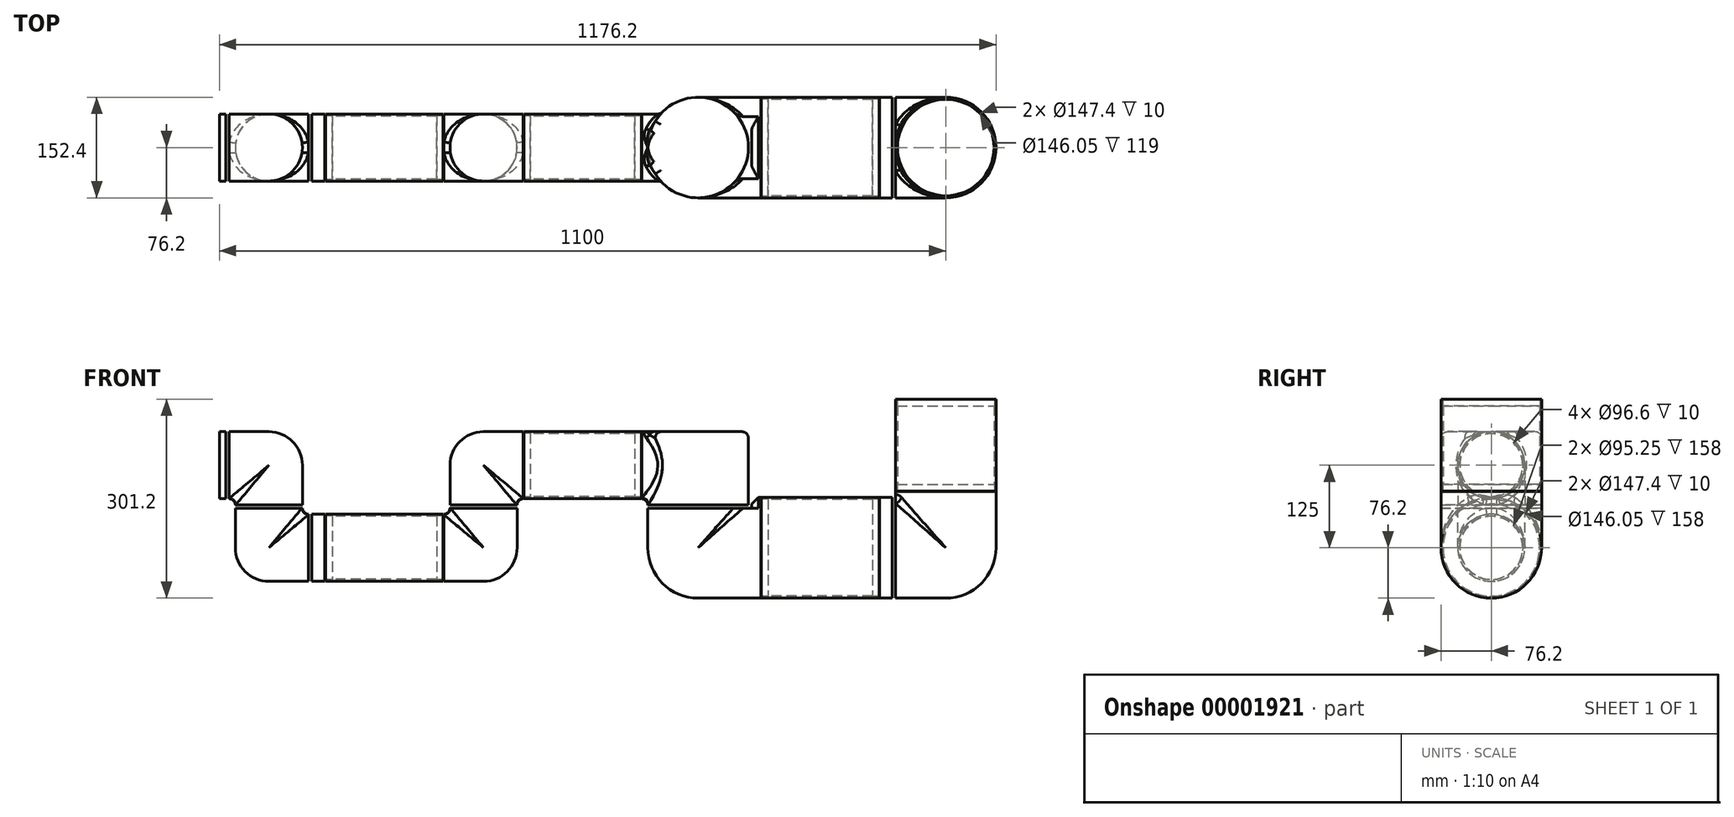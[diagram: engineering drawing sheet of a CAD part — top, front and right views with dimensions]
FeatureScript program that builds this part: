
annotation { "Feature Type Name" : "Feature", "Feature Type Description" : "" }
export const myFeature = defineFeature(function(context is Context, id is Id, definition is map)
    precondition{}
    {
        {
            var Q0;
            Q0=qCreatedBy(makeId("Front.planeOp"),FACE);
            var sketch = newSketch(context, id + "F0", { "sketchPlane" : qUnion([Q0])});
            skLineSegment(sketch, "E0", {"start": v(0, 0) * mm, "end": v(0, -225) * mm, "construction": true});
            skLineSegment(sketch, "E1", {"start": v(0, -225) * mm, "end": v(-375, -225) * mm, "construction": true});
            skLineSegment(sketch, "E2", {"start": v(-375, -225) * mm, "end": v(-375, -100) * mm, "construction": true});
            skLineSegment(sketch, "E3", {"start": v(-375, -100) * mm, "end": v(-700, -100) * mm, "construction": true});
            skLineSegment(sketch, "E4", {"start": v(-700, -100) * mm, "end": v(-700, -225) * mm, "construction": true});
            skLineSegment(sketch, "E5", {"start": v(-700, -225) * mm, "end": v(-1025, -225) * mm, "construction": true});
            skLineSegment(sketch, "E6", {"start": v(-1025, -225) * mm, "end": v(-1025, -100) * mm, "construction": true});
            skLineSegment(sketch, "E7", {"start": v(-1025, -100) * mm, "end": v(-1100, -100) * mm, "construction": true});
            skSolve(sketch);
        }
        {
            var Q0;
            Q0=qCreatedBy(makeId("Top.planeOp"),FACE);
            var Q1;
            Q1=sQuery(id+"F0.wireOp",VERTEX,"E1.start");
            cPlane(context, id + "F1", {"entities" : qUnion([Q0, Q1]), "cplaneType" : CPlaneType.PLANE_POINT, "offset" : 152.4 * mm, "width" : 152.4 * mm, "height" : 152.4 * mm});
        }
        {
            var Q0;
            Q0=qCreatedBy(makeId("Right.planeOp"),FACE);
            var Q1;
            Q1=sQuery(id+"F0.wireOp",VERTEX,"E2.start");
            cPlane(context, id + "F2", {"entities" : qUnion([Q0, Q1]), "cplaneType" : CPlaneType.PLANE_POINT, "offset" : 152.4 * mm, "width" : 152.4 * mm, "height" : 152.4 * mm});
        }
        {
            var Q0;
            Q0=qCreatedBy(makeId("Top.planeOp"),FACE);
            var Q1;
            Q1=sQuery(id+"F0.wireOp",VERTEX,"E3.start");
            cPlane(context, id + "F3", {"entities" : qUnion([Q0, Q1]), "cplaneType" : CPlaneType.PLANE_POINT, "offset" : 152.4 * mm, "width" : 152.4 * mm, "height" : 152.4 * mm});
        }
        {
            var Q0;
            Q0=qCreatedBy(makeId("Right.planeOp"),FACE);
            var Q1;
            Q1=sQuery(id+"F0.wireOp",VERTEX,"E4.end");
            cPlane(context, id + "F4", {"entities" : qUnion([Q0, Q1]), "cplaneType" : CPlaneType.PLANE_POINT, "offset" : 152.4 * mm, "width" : 152.4 * mm, "height" : 152.4 * mm});
        }
        {
            var Q0;
            Q0=qCreatedBy(makeId("Top.planeOp"),FACE);
            var Q1;
            Q1=sQuery(id+"F0.wireOp",VERTEX,"E4.end");
            cPlane(context, id + "F5", {"entities" : qUnion([Q0, Q1]), "cplaneType" : CPlaneType.PLANE_POINT, "offset" : 152.4 * mm, "width" : 152.4 * mm, "height" : 152.4 * mm});
        }
        {
            var Q0;
            Q0=qCreatedBy(makeId("Right.planeOp"),FACE);
            var Q1;
            Q1=sQuery(id+"F0.wireOp",VERTEX,"E6.start");
            cPlane(context, id + "F6", {"entities" : qUnion([Q0, Q1]), "cplaneType" : CPlaneType.PLANE_POINT, "offset" : 152.4 * mm, "width" : 152.4 * mm, "height" : 152.4 * mm});
        }
        {
            var Q0;
            Q0=qCreatedBy(makeId("Top.planeOp"),FACE);
            var Q1;
            Q1=sQuery(id+"F0.wireOp",VERTEX,"E6.end");
            cPlane(context, id + "F7", {"entities" : qUnion([Q0, Q1]), "cplaneType" : CPlaneType.PLANE_POINT, "offset" : 152.4 * mm, "width" : 152.4 * mm, "height" : 152.4 * mm});
        }
        {
            var Q0;
            Q0=qCreatedBy(makeId("Right.planeOp"),FACE);
            var Q1;
            Q1=sQuery(id+"F0.wireOp",VERTEX,"E7.end");
            cPlane(context, id + "F8", {"entities" : qUnion([Q0, Q1]), "cplaneType" : CPlaneType.PLANE_POINT, "offset" : 152.4 * mm, "width" : 152.4 * mm, "height" : 152.4 * mm});
        }
        {
            var Q0;
            Q0=qCreatedBy(makeId("Top.planeOp"),FACE);
            var sketch = newSketch(context, id + "F9", { "sketchPlane" : qUnion([Q0])});
            skCircle(sketch, "E8", {"center": v(0, 0) * mm, "radius": 76.2 * mm});
            skSolve(sketch);
        }
        {
            var Q0;
            Q0=makeQuery(id+"F9.imprint","IMPRINT",FACE,{"disambiguationData":[TD([[makeQuery(id+"F9.imprint","IMPRINT",EDGE,{"derivedFrom":sQuery(id+"F9.wireOp",EDGE,"E8")}),1.0]])]});
            var Q1;
            Q1=qCreatedBy(id+"F1.planeOp",FACE);
            extrude(context, id + "F10", {"entities" : qUnion([Q0]), "endBound" : BoundingType.UP_TO_SURFACE, "oppositeDirection" : true, "endBoundEntityFace" : qUnion([Q1]), "depth" : 25.4 * mm});
        }
        {
            var Q0;
            Q0=qCreatedBy(makeId("Right.planeOp"),FACE);
            var sketch = newSketch(context, id + "F11", { "sketchPlane" : qUnion([Q0])});
            skCircle(sketch, "E9", {"center": v(0, -225) * mm, "radius": 76.2 * mm});
            skSolve(sketch);
        }
        {
            var Q0;
            Q0 = qSketchRegion(id + "F11", true);
            var Q1;
            Q1=qCreatedBy(id+"F2.planeOp",FACE);
            extrude(context, id + "F12", {"entities" : qUnion([Q0]), "operationType" : NewBodyOperationType.ADD, "endBound" : BoundingType.UP_TO_SURFACE, "oppositeDirection" : true, "endBoundEntityFace" : qUnion([Q1]), "depth" : 25.4 * mm});
        }
        {
            var Q0;
            Q0=qCreatedBy(id+"F1.planeOp",FACE);
            var sketch = newSketch(context, id + "F13", { "sketchPlane" : qUnion([Q0])});
            skCircle(sketch, "E10", {"center": v(-375, 0) * mm, "radius": 76.2 * mm});
            skSolve(sketch);
        }
        {
            var Q0;
            Q0=makeQuery(id+"F13.imprint","IMPRINT",FACE,{"disambiguationData":[TD([[makeQuery(id+"F13.imprint","IMPRINT",EDGE,{"derivedFrom":sQuery(id+"F13.wireOp",EDGE,"E10")}),1.0]])]});
            var Q1;
            Q1=qCreatedBy(id+"F3.planeOp",FACE);
            extrude(context, id + "F14", {"entities" : qUnion([Q0]), "operationType" : NewBodyOperationType.ADD, "endBound" : BoundingType.UP_TO_SURFACE, "endBoundEntityFace" : qUnion([Q1]), "depth" : 25.4 * mm});
        }
        {
            var Q0;
            Q0=qCreatedBy(id+"F2.planeOp",FACE);
            var sketch = newSketch(context, id + "F15", { "sketchPlane" : qUnion([Q0])});
            skCircle(sketch, "E11", {"center": v(0, -100) * mm, "radius": 50.8 * mm});
            skSolve(sketch);
        }
        {
            var Q0;
            Q0 = qSketchRegion(id + "F15", true);
            var Q1;
            Q1=qCreatedBy(id+"F4.planeOp",FACE);
            extrude(context, id + "F16", {"entities" : qUnion([Q0]), "operationType" : NewBodyOperationType.ADD, "endBound" : BoundingType.UP_TO_SURFACE, "oppositeDirection" : true, "endBoundEntityFace" : qUnion([Q1]), "depth" : 25.4 * mm});
        }
        {
            var Q0;
            Q0=qCreatedBy(id+"F3.planeOp",FACE);
            var sketch = newSketch(context, id + "F17", { "sketchPlane" : qUnion([Q0])});
            skCircle(sketch, "E12", {"center": v(-700, 0) * mm, "radius": 50.8 * mm});
            skSolve(sketch);
        }
        {
            var Q0;
            Q0 = qSketchRegion(id + "F17", true);
            var Q1;
            Q1=qCreatedBy(id+"F5.planeOp",FACE);
            extrude(context, id + "F18", {"entities" : qUnion([Q0]), "operationType" : NewBodyOperationType.ADD, "endBound" : BoundingType.UP_TO_SURFACE, "oppositeDirection" : true, "endBoundEntityFace" : qUnion([Q1]), "depth" : 25.4 * mm});
        }
        {
            var Q0;
            Q0=qCreatedBy(id+"F4.planeOp",FACE);
            var sketch = newSketch(context, id + "F19", { "sketchPlane" : qUnion([Q0])});
            skCircle(sketch, "E13", {"center": v(0, -225) * mm, "radius": 50.8 * mm});
            skSolve(sketch);
        }
        {
            var Q0;
            Q0 = qSketchRegion(id + "F19", true);
            var Q1;
            Q1=qCreatedBy(id+"F6.planeOp",FACE);
            extrude(context, id + "F20", {"entities" : qUnion([Q0]), "operationType" : NewBodyOperationType.ADD, "endBound" : BoundingType.UP_TO_SURFACE, "oppositeDirection" : true, "endBoundEntityFace" : qUnion([Q1]), "depth" : 25.4 * mm});
        }
        {
            var Q0;
            Q0=qCreatedBy(id+"F5.planeOp",FACE);
            var sketch = newSketch(context, id + "F21", { "sketchPlane" : qUnion([Q0])});
            skCircle(sketch, "E14", {"center": v(-1025, 0) * mm, "radius": 50.8 * mm});
            skSolve(sketch);
        }
        {
            var Q0;
            Q0 = qSketchRegion(id + "F21", true);
            var Q1;
            Q1=qCreatedBy(id+"F7.planeOp",FACE);
            extrude(context, id + "F22", {"entities" : qUnion([Q0]), "operationType" : NewBodyOperationType.ADD, "endBound" : BoundingType.UP_TO_SURFACE, "endBoundEntityFace" : qUnion([Q1]), "depth" : 25.4 * mm});
        }
        {
            var Q0;
            Q0=qCreatedBy(id+"F6.planeOp",FACE);
            var sketch = newSketch(context, id + "F23", { "sketchPlane" : qUnion([Q0])});
            skCircle(sketch, "E15", {"center": v(0, -100) * mm, "radius": 50.8 * mm});
            skSolve(sketch);
        }
        {
            var Q0;
            Q0 = qSketchRegion(id + "F23", true);
            var Q1;
            Q1=qCreatedBy(id+"F8.planeOp",FACE);
            extrude(context, id + "F24", {"entities" : qUnion([Q0]), "operationType" : NewBodyOperationType.ADD, "endBound" : BoundingType.UP_TO_SURFACE, "oppositeDirection" : true, "endBoundEntityFace" : qUnion([Q1]), "depth" : 25.4 * mm});
        }
        {
            var Q0;
            Q0=makeQuery(id+"F10.opExtrude","CAP_FACE",FACE,{"disambiguationData":[OSD([sQuery(id+"F9.wireOp",EDGE,"E8")])],"isStart":false});
            var Q1;
            Q1=makeQuery(id+"F12.boolean.opBoolean","INTERSECT",EDGE,{"derivedFrom":[makeQuery(id+"F10.opExtrude","CAP_FACE",FACE,{"disambiguationData":[OSD([sQuery(id+"F9.wireOp",EDGE,"E8")])],"isStart":false}),makeQuery(id+"F12.opExtrude","CAP_FACE",FACE,{"disambiguationData":[OSD([sQuery(id+"F11.wireOp",EDGE,"E9")])],"isStart":true})]});
            revolve(context, id + "F25", {"operationType" : NewBodyOperationType.ADD, "entities" : qUnion([Q0]), "axis" : qUnion([Q1]), "revolveType" : RevolveType.ONE_DIRECTION, "angle" : 90 * degree});
        }
        {
            var Q0;
            Q0=makeQuery(id+"F12.opExtrude","CAP_FACE",FACE,{"disambiguationData":[OSD([sQuery(id+"F11.wireOp",EDGE,"E9")])],"isStart":false});
            var Q1;
            Q1=makeQuery(id+"F14.boolean.opBoolean","INTERSECT",EDGE,{"derivedFrom":[makeQuery(id+"F12.opExtrude","CAP_FACE",FACE,{"disambiguationData":[OSD([sQuery(id+"F11.wireOp",EDGE,"E9")])],"isStart":false}),makeQuery(id+"F14.opExtrude","CAP_FACE",FACE,{"disambiguationData":[OSD([sQuery(id+"F13.wireOp",EDGE,"E10")])],"isStart":true})]});
            revolve(context, id + "F26", {"operationType" : NewBodyOperationType.ADD, "entities" : qUnion([Q0]), "axis" : qUnion([Q1]), "revolveType" : RevolveType.ONE_DIRECTION, "oppositeDirection" : true, "angle" : 90 * degree});
        }
        {
            var Q0;
            Q0=makeQuery(id+"F16.opExtrude","CAP_FACE",FACE,{"disambiguationData":[OSD([sQuery(id+"F15.wireOp",EDGE,"E11")])],"isStart":false});
            var Q1;
            Q1=makeQuery(id+"F18.boolean.opBoolean","INTERSECT",EDGE,{"derivedFrom":[makeQuery(id+"F16.opExtrude","CAP_FACE",FACE,{"disambiguationData":[OSD([sQuery(id+"F15.wireOp",EDGE,"E11")])],"isStart":false}),makeQuery(id+"F18.opExtrude","CAP_FACE",FACE,{"disambiguationData":[OSD([sQuery(id+"F17.wireOp",EDGE,"E12")])],"isStart":true})]});
            revolve(context, id + "F27", {"operationType" : NewBodyOperationType.ADD, "entities" : qUnion([Q0]), "axis" : qUnion([Q1]), "revolveType" : RevolveType.ONE_DIRECTION, "angle" : 90 * degree});
        }
        {
            var Q0;
            Q0=makeQuery(id+"F18.opExtrude","CAP_FACE",FACE,{"disambiguationData":[OSD([sQuery(id+"F17.wireOp",EDGE,"E12")])],"isStart":false});
            var Q1;
            Q1=makeQuery(id+"F20.boolean.opBoolean","INTERSECT",EDGE,{"derivedFrom":[makeQuery(id+"F18.opExtrude","CAP_FACE",FACE,{"disambiguationData":[OSD([sQuery(id+"F17.wireOp",EDGE,"E12")])],"isStart":false}),makeQuery(id+"F20.opExtrude","CAP_FACE",FACE,{"disambiguationData":[OSD([sQuery(id+"F19.wireOp",EDGE,"E13")])],"isStart":true})]});
            revolve(context, id + "F28", {"operationType" : NewBodyOperationType.ADD, "entities" : qUnion([Q0]), "axis" : qUnion([Q1]), "revolveType" : RevolveType.ONE_DIRECTION, "angle" : 90 * degree});
        }
        {
            var Q0;
            Q0=makeQuery(id+"F20.opExtrude","CAP_FACE",FACE,{"disambiguationData":[OSD([sQuery(id+"F19.wireOp",EDGE,"E13")])],"isStart":false});
            var Q1;
            Q1=makeQuery(id+"F22.boolean.opBoolean","INTERSECT",EDGE,{"derivedFrom":[makeQuery(id+"F20.opExtrude","CAP_FACE",FACE,{"disambiguationData":[OSD([sQuery(id+"F19.wireOp",EDGE,"E13")])],"isStart":false}),makeQuery(id+"F22.opExtrude","CAP_FACE",FACE,{"disambiguationData":[OSD([sQuery(id+"F21.wireOp",EDGE,"E14")])],"isStart":true})]});
            revolve(context, id + "F29", {"operationType" : NewBodyOperationType.ADD, "entities" : qUnion([Q0]), "axis" : qUnion([Q1]), "revolveType" : RevolveType.ONE_DIRECTION, "oppositeDirection" : true, "angle" : 90 * degree});
        }
        {
            var Q0;
            Q0=makeQuery(id+"F22.opExtrude","CAP_FACE",FACE,{"disambiguationData":[OSD([sQuery(id+"F21.wireOp",EDGE,"E14")])],"isStart":false});
            var Q1;
            Q1=makeQuery(id+"F24.boolean.opBoolean","INTERSECT",EDGE,{"derivedFrom":[makeQuery(id+"F22.opExtrude","CAP_FACE",FACE,{"disambiguationData":[OSD([sQuery(id+"F21.wireOp",EDGE,"E14")])],"isStart":false}),makeQuery(id+"F24.opExtrude","CAP_FACE",FACE,{"disambiguationData":[OSD([sQuery(id+"F23.wireOp",EDGE,"E15")])],"isStart":true})]});
            revolve(context, id + "F30", {"operationType" : NewBodyOperationType.ADD, "entities" : qUnion([Q0]), "axis" : qUnion([Q1]), "revolveType" : RevolveType.ONE_DIRECTION, "oppositeDirection" : true, "angle" : 90 * degree});
        }
        {
            var Q0;
            Q0=qCreatedBy(id+"F3.planeOp",FACE);
            var sketch = newSketch(context, id + "F31", { "sketchPlane" : qUnion([Q0])});
            skCircle(sketch, "E16", {"center": v(-375, 0) * mm, "radius": 76.2 * mm});
            skSolve(sketch);
        }
        {
            var Q0;
            Q0 = qSketchRegion(id + "F31", true);
            var Q1;
            Q1=makeQuery(id+"F16.opExtrude","SWEPT_FACE",FACE,{"disambiguationData":[OSD([sQuery(id+"F15.wireOp",EDGE,"E11")])]});
            extrude(context, id + "F32", {"entities" : qUnion([Q0]), "operationType" : NewBodyOperationType.ADD, "endBoundEntity" : qUnion([Q1]), "depth" : 50.8 * mm});
        }
        {
            var Q0;
            Q0=qCreatedBy(makeId("Front.planeOp"),FACE);
            var sketch = newSketch(context, id + "F33", { "sketchPlane" : qUnion([Q0])});
            skLineSegment(sketch, "E17.bottom", {"start": v(-81.2, -225) * mm, "end": v(-76.2, -225) * mm});
            skLineSegment(sketch, "E17.top", {"start": v(-81.2, -301.2) * mm, "end": v(-76.2, -301.2) * mm});
            skLineSegment(sketch, "E17.left", {"start": v(-81.2, -225) * mm, "end": v(-81.2, -301.2) * mm});
            skLineSegment(sketch, "E17.right", {"start": v(-76.2, -225) * mm, "end": v(-76.2, -301.2) * mm});
            skLineSegment(sketch, "E18.bottom", {"start": v(-451.2, -160) * mm, "end": v(-375, -160) * mm});
            skLineSegment(sketch, "E18.top", {"start": v(-451.2, -165) * mm, "end": v(-375, -165) * mm});
            skLineSegment(sketch, "E18.left", {"start": v(-451.2, -160) * mm, "end": v(-451.2, -165) * mm});
            skLineSegment(sketch, "E18.right", {"start": v(-375, -160) * mm, "end": v(-375, -165) * mm});
            skLineSegment(sketch, "E19.bottom", {"start": v(-700, -160) * mm, "end": v(-649.2, -160) * mm});
            skLineSegment(sketch, "E19.top", {"start": v(-700, -165) * mm, "end": v(-649.2, -165) * mm});
            skLineSegment(sketch, "E19.left", {"start": v(-700, -160) * mm, "end": v(-700, -165) * mm});
            skLineSegment(sketch, "E19.right", {"start": v(-649.2, -160) * mm, "end": v(-649.2, -165) * mm});
            skLineSegment(sketch, "E20.bottom", {"start": v(-960, -225) * mm, "end": v(-965, -225) * mm});
            skLineSegment(sketch, "E20.top", {"start": v(-960, -174.2) * mm, "end": v(-965, -174.2) * mm});
            skLineSegment(sketch, "E20.left", {"start": v(-960, -225) * mm, "end": v(-960, -174.2) * mm});
            skLineSegment(sketch, "E20.right", {"start": v(-965, -225) * mm, "end": v(-965, -174.2) * mm});
            skLineSegment(sketch, "E21.bottom", {"start": v(-1075.8, -160) * mm, "end": v(-1025, -160) * mm});
            skLineSegment(sketch, "E21.top", {"start": v(-1075.8, -165) * mm, "end": v(-1025, -165) * mm});
            skLineSegment(sketch, "E21.left", {"start": v(-1075.8, -160) * mm, "end": v(-1075.8, -165) * mm});
            skLineSegment(sketch, "E21.right", {"start": v(-1025, -160) * mm, "end": v(-1025, -165) * mm});
            skLineSegment(sketch, "E22.bottom", {"start": v(-1090, -100) * mm, "end": v(-1085, -100) * mm});
            skLineSegment(sketch, "E22.top", {"start": v(-1090, -49.2) * mm, "end": v(-1085, -49.2) * mm});
            skLineSegment(sketch, "E22.left", {"start": v(-1090, -100) * mm, "end": v(-1090, -49.2) * mm});
            skLineSegment(sketch, "E22.right", {"start": v(-1085, -100) * mm, "end": v(-1085, -49.2) * mm});
            skLineSegment(sketch, "E23.0", {"start": v(0, -148.8) * mm, "end": v(0, -301.2) * mm, "construction": true});
            skLineSegment(sketch, "E24.0", {"start": v(-76.2, 0) * mm, "end": v(76.2, 0) * mm, "construction": true});
            skLineSegment(sketch, "E25.0", {"start": v(-451.2, -225) * mm, "end": v(-298.8, -225) * mm, "construction": true});
            skLineSegment(sketch, "E26.0", {"start": v(-700, -174.2) * mm, "end": v(-700, -275.8) * mm, "construction": true});
            skLineSegment(sketch, "E27.0", {"start": v(-1075.8, -225) * mm, "end": v(-974.2, -225) * mm, "construction": true});
            skLineSegment(sketch, "E28.0", {"start": v(-1025, -49.2) * mm, "end": v(-1025, -150.8) * mm, "construction": true});
            skLineSegment(sketch, "E29.0", {"start": v(-750.8, -100) * mm, "end": v(-649.2, -100) * mm, "construction": true});
            skSolve(sketch);
        }
        {
            var Q0;
            Q0=makeQuery(id+"F33.imprint","IMPRINT",FACE,{"disambiguationData":[TD([[makeQuery(id+"F33.imprint","IMPRINT",EDGE,{"derivedFrom":sQuery(id+"F33.wireOp",EDGE,"E17.bottom")}),-1.0]])]});
            var Q1;
            Q1=sQuery(id+"F0.wireOp",EDGE,"E1");
            revolve(context, id + "F34", {"operationType" : NewBodyOperationType.REMOVE, "entities" : qUnion([Q0]), "axis" : qUnion([Q1]), "revolveType" : RevolveType.FULL, "oppositeDirection" : true});
        }
        {
            var Q0;
            Q0=makeQuery(id+"F33.imprint","IMPRINT",FACE,{"disambiguationData":[TD([[makeQuery(id+"F33.imprint","IMPRINT",EDGE,{"derivedFrom":sQuery(id+"F33.wireOp",EDGE,"E18.bottom")}),-1.0]])]});
            var Q1;
            Q1=sQuery(id+"F0.wireOp",EDGE,"E2");
            revolve(context, id + "F35", {"operationType" : NewBodyOperationType.REMOVE, "entities" : qUnion([Q0]), "axis" : qUnion([Q1]), "revolveType" : RevolveType.FULL, "oppositeDirection" : true});
        }
        {
            var Q0;
            Q0=qCreatedBy(id+"F3.planeOp",FACE);
            var sketch = newSketch(context, id + "F36", { "sketchPlane" : qUnion([Q0])});
            skCircle(sketch, "E30", {"center": v(-375, 0) * mm, "radius": 76.2 * mm});
            skLineSegment(sketch, "E31.bottom", {"start": v(-375, 159.28) * mm, "end": v(-293.8, 159.28) * mm});
            skLineSegment(sketch, "E31.top", {"start": v(-375, -164.24) * mm, "end": v(-293.8, -164.24) * mm});
            skLineSegment(sketch, "E31.left", {"start": v(-375, 159.28) * mm, "end": v(-375, -164.24) * mm});
            skLineSegment(sketch, "E31.right", {"start": v(-293.8, 159.28) * mm, "end": v(-293.8, -164.24) * mm});
            skSolve(sketch);
        }
        {
            var Q0;
            {var subQ5=sQuery(id+"F36.wireOp",EDGE,"E31.bottom");Q0=makeQuery(id+"F36.imprint","IMPRINT",FACE,{"disambiguationData":[TD([[makeQuery(id+"F36.imprint","IMPRINT",EDGE,{"derivedFrom":subQ5}),-1.0]])]});}
            var Q1;
            Q1=makeQuery(id+"F35.boolean.opBoolean","COPY",FACE,{"derivedFrom":makeQuery(id+"F35.opRevolve","SWEPT_FACE",FACE,{"disambiguationData":[OSD([sQuery(id+"F33.wireOp",EDGE,"E18.top")])]})});
            extrude(context, id + "F37", {"entities" : qUnion([Q0]), "operationType" : NewBodyOperationType.REMOVE, "endBound" : BoundingType.UP_TO_SURFACE, "oppositeDirection" : true, "endBoundEntityFace" : qUnion([Q1]), "depth" : 25 * mm});
        }
        {
            var Q0;
            Q0=makeQuery(id+"F33.imprint","IMPRINT",FACE,{"disambiguationData":[TD([[makeQuery(id+"F33.imprint","IMPRINT",EDGE,{"derivedFrom":sQuery(id+"F33.wireOp",EDGE,"E19.bottom")}),-1.0]])]});
            var Q1;
            Q1=sQuery(id+"F0.wireOp",EDGE,"E4");
            revolve(context, id + "F38", {"operationType" : NewBodyOperationType.REMOVE, "entities" : qUnion([Q0]), "axis" : qUnion([Q1]), "revolveType" : RevolveType.FULL, "oppositeDirection" : true});
        }
        {
            var Q0;
            Q0=makeQuery(id+"F33.imprint","IMPRINT",FACE,{"disambiguationData":[TD([[makeQuery(id+"F33.imprint","IMPRINT",EDGE,{"derivedFrom":sQuery(id+"F33.wireOp",EDGE,"E20.bottom")}),-1.0]])]});
            var Q1;
            Q1=sQuery(id+"F0.wireOp",EDGE,"E5");
            revolve(context, id + "F39", {"operationType" : NewBodyOperationType.REMOVE, "entities" : qUnion([Q0]), "axis" : qUnion([Q1]), "revolveType" : RevolveType.FULL, "oppositeDirection" : true});
        }
        {
            var Q0;
            Q0=makeQuery(id+"F33.imprint","IMPRINT",FACE,{"disambiguationData":[TD([[makeQuery(id+"F33.imprint","IMPRINT",EDGE,{"derivedFrom":sQuery(id+"F33.wireOp",EDGE,"E21.bottom")}),-1.0]])]});
            var Q1;
            Q1=sQuery(id+"F0.wireOp",EDGE,"E6");
            revolve(context, id + "F40", {"operationType" : NewBodyOperationType.REMOVE, "entities" : qUnion([Q0]), "axis" : qUnion([Q1]), "revolveType" : RevolveType.FULL, "oppositeDirection" : true});
        }
        {
            var Q0;
            Q0=makeQuery(id+"F33.imprint","IMPRINT",FACE,{"disambiguationData":[TD([[makeQuery(id+"F33.imprint","IMPRINT",EDGE,{"derivedFrom":sQuery(id+"F33.wireOp",EDGE,"E22.bottom")}),1.0]])]});
            var Q1;
            Q1=sQuery(id+"F0.wireOp",EDGE,"E7");
            revolve(context, id + "F41", {"operationType" : NewBodyOperationType.REMOVE, "entities" : qUnion([Q0]), "axis" : qUnion([Q1]), "revolveType" : RevolveType.FULL, "oppositeDirection" : true});
        }
        {
            var Q0;
            Q0=qCreatedBy(makeId("Front.planeOp"),FACE);
            var sketch = newSketch(context, id + "F42", { "sketchPlane" : qUnion([Q0])});
            skLineSegment(sketch, "E32.0", {"start": v(-76.2, 0) * mm, "end": v(76.2, 0) * mm, "construction": true});
            skLineSegment(sketch, "E33", {"start": v(73.7, 0) * mm, "end": v(73.7, -10) * mm});
            skLineSegment(sketch, "E34", {"start": v(73.7, -10) * mm, "end": v(73.02, -10) * mm});
            skLineSegment(sketch, "E35", {"start": v(73.02, -10) * mm, "end": v(73.03, -129) * mm});
            skLineSegment(sketch, "E36", {"start": v(73.03, -129) * mm, "end": v(73.7, -129) * mm});
            skLineSegment(sketch, "E37", {"start": v(73.7, -129) * mm, "end": v(73.7, -139) * mm});
            skLineSegment(sketch, "E38", {"start": v(73.7, -139) * mm, "end": v(76.2, -139) * mm});
            skLineSegment(sketch, "E39", {"start": v(73.7, 0) * mm, "end": v(0, 0) * mm});
            skLineSegment(sketch, "E40", {"start": v(0, 0) * mm, "end": v(0, -140) * mm});
            skLineSegment(sketch, "E41", {"start": v(0, -140) * mm, "end": v(76.2, -140) * mm});
            skLineSegment(sketch, "E42", {"start": v(76.2, -140) * mm, "end": v(76.2, -139) * mm});
            skLineSegment(sketch, "E43", {"start": v(-280, -225) * mm, "end": v(-280, -148.8) * mm});
            skLineSegment(sketch, "E44", {"start": v(-280, -148.8) * mm, "end": v(-279, -148.8) * mm});
            skLineSegment(sketch, "E45", {"start": v(-279, -148.8) * mm, "end": v(-279, -151.3) * mm});
            skLineSegment(sketch, "E46", {"start": v(-279, -151.3) * mm, "end": v(-269, -151.3) * mm});
            skLineSegment(sketch, "E47", {"start": v(-269, -151.3) * mm, "end": v(-269, -151.97) * mm});
            skLineSegment(sketch, "E48", {"start": v(-269, -151.97) * mm, "end": v(-111, -151.97) * mm});
            skLineSegment(sketch, "E49", {"start": v(-111, -151.97) * mm, "end": v(-111, -151.3) * mm});
            skLineSegment(sketch, "E50", {"start": v(-111, -151.3) * mm, "end": v(-101, -151.3) * mm});
            skLineSegment(sketch, "E51", {"start": v(-101, -151.3) * mm, "end": v(-101, -148.8) * mm});
            skLineSegment(sketch, "E52", {"start": v(-101, -148.8) * mm, "end": v(-100, -148.8) * mm});
            skLineSegment(sketch, "E53", {"start": v(-100, -148.8) * mm, "end": v(-100, -225) * mm});
            skLineSegment(sketch, "E54", {"start": v(-100, -225) * mm, "end": v(-280, -225) * mm});
            skLineSegment(sketch, "E55.0", {"start": v(0, -148.8) * mm, "end": v(0, -301.2) * mm, "construction": true});
            skLineSegment(sketch, "E56", {"start": v(-640, -49.2) * mm, "end": v(-640, -100) * mm});
            skLineSegment(sketch, "E57", {"start": v(-640, -100) * mm, "end": v(-460, -100) * mm});
            skLineSegment(sketch, "E58", {"start": v(-460, -100) * mm, "end": v(-460, -49.2) * mm});
            skLineSegment(sketch, "E59", {"start": v(-460, -49.2) * mm, "end": v(-461, -49.2) * mm});
            skLineSegment(sketch, "E60", {"start": v(-461, -49.2) * mm, "end": v(-461, -51.7) * mm});
            skLineSegment(sketch, "E61", {"start": v(-461, -51.7) * mm, "end": v(-471, -51.7) * mm});
            skLineSegment(sketch, "E62", {"start": v(-471, -51.7) * mm, "end": v(-471, -52.38) * mm});
            skLineSegment(sketch, "E63", {"start": v(-471, -52.38) * mm, "end": v(-629, -52.38) * mm});
            skLineSegment(sketch, "E64", {"start": v(-629, -52.38) * mm, "end": v(-629, -51.7) * mm});
            skLineSegment(sketch, "E65", {"start": v(-629, -51.7) * mm, "end": v(-639, -51.7) * mm});
            skLineSegment(sketch, "E66", {"start": v(-639, -51.7) * mm, "end": v(-639, -49.2) * mm});
            skLineSegment(sketch, "E67", {"start": v(-639, -49.2) * mm, "end": v(-640, -49.2) * mm});
            skLineSegment(sketch, "E68.0", {"start": v(-375, -49.2) * mm, "end": v(-375, -150.8) * mm, "construction": true});
            skLineSegment(sketch, "E69", {"start": v(-940, -225) * mm, "end": v(-940, -174.2) * mm});
            skLineSegment(sketch, "E70", {"start": v(-940, -174.2) * mm, "end": v(-939, -174.2) * mm});
            skLineSegment(sketch, "E71", {"start": v(-939, -174.2) * mm, "end": v(-939, -176.7) * mm});
            skLineSegment(sketch, "E72", {"start": v(-939, -176.7) * mm, "end": v(-929, -176.7) * mm});
            skLineSegment(sketch, "E73", {"start": v(-929, -176.7) * mm, "end": v(-929, -177.38) * mm});
            skLineSegment(sketch, "E74", {"start": v(-929, -177.38) * mm, "end": v(-771, -177.38) * mm});
            skLineSegment(sketch, "E75", {"start": v(-771, -177.38) * mm, "end": v(-771, -176.7) * mm});
            skLineSegment(sketch, "E76", {"start": v(-771, -176.7) * mm, "end": v(-761, -176.7) * mm});
            skLineSegment(sketch, "E77", {"start": v(-761, -176.7) * mm, "end": v(-761, -174.2) * mm});
            skLineSegment(sketch, "E78", {"start": v(-761, -174.2) * mm, "end": v(-760, -174.2) * mm});
            skLineSegment(sketch, "E79", {"start": v(-760, -174.2) * mm, "end": v(-760, -225) * mm});
            skLineSegment(sketch, "E80", {"start": v(-760, -225) * mm, "end": v(-940, -225) * mm});
            skLineSegment(sketch, "E81.0", {"start": v(-700, -174.2) * mm, "end": v(-700, -275.8) * mm, "construction": true});
            skSolve(sketch);
        }
        {
            var Q0;
            Q0=makeQuery(id+"F42.imprint","IMPRINT",FACE,{"disambiguationData":[TD([[makeQuery(id+"F42.imprint","IMPRINT",EDGE,{"derivedFrom":sQuery(id+"F42.wireOp",EDGE,"E33")}),-1.0]])]});
            var Q1;
            Q1=sQuery(id+"F0.wireOp",EDGE,"E0");
            revolve(context, id + "F43", {"operationType" : NewBodyOperationType.REMOVE, "entities" : qUnion([Q0]), "axis" : qUnion([Q1]), "revolveType" : RevolveType.FULL, "oppositeDirection" : true});
        }
        {
            var Q0;
            Q0=makeQuery(id+"F42.imprint","IMPRINT",FACE,{"disambiguationData":[TD([[makeQuery(id+"F42.imprint","IMPRINT",EDGE,{"derivedFrom":sQuery(id+"F42.wireOp",EDGE,"E43")}),-1.0]])]});
            var Q1;
            Q1=sQuery(id+"F0.wireOp",EDGE,"E1");
            revolve(context, id + "F44", {"operationType" : NewBodyOperationType.REMOVE, "entities" : qUnion([Q0]), "axis" : qUnion([Q1]), "revolveType" : RevolveType.FULL, "oppositeDirection" : true});
        }
        {
            var Q0;
            Q0=makeQuery(id+"F42.imprint","IMPRINT",FACE,{"disambiguationData":[TD([[makeQuery(id+"F42.imprint","IMPRINT",EDGE,{"derivedFrom":sQuery(id+"F42.wireOp",EDGE,"E69")}),-1.0]])]});
            var Q1;
            Q1=sQuery(id+"F0.wireOp",EDGE,"E5");
            revolve(context, id + "F45", {"operationType" : NewBodyOperationType.REMOVE, "entities" : qUnion([Q0]), "axis" : qUnion([Q1]), "revolveType" : RevolveType.FULL, "oppositeDirection" : true});
        }
        {
            var Q0;
            Q0=makeQuery(id+"F42.imprint","IMPRINT",FACE,{"disambiguationData":[TD([[makeQuery(id+"F42.imprint","IMPRINT",EDGE,{"derivedFrom":sQuery(id+"F42.wireOp",EDGE,"E56")}),1.0]])]});
            var Q1;
            Q1=sQuery(id+"F0.wireOp",EDGE,"E3");
            revolve(context, id + "F46", {"operationType" : NewBodyOperationType.REMOVE, "entities" : qUnion([Q0]), "axis" : qUnion([Q1]), "revolveType" : RevolveType.FULL, "oppositeDirection" : true});
        }
        {
            var Q0;
            Q0=makeQuery(id+"F24.boolean.opBoolean","INTERSECT",EDGE,{"derivedFrom":[makeQuery(id+"F22.opExtrude","SWEPT_FACE",FACE,{"disambiguationData":[OSD([sQuery(id+"F21.wireOp",EDGE,"E14")])]}),makeQuery(id+"F24.opExtrude","SWEPT_FACE",FACE,{"disambiguationData":[OSD([sQuery(id+"F23.wireOp",EDGE,"E15")])]})]});
            var Q1;
            Q1=makeQuery(id+"F22.boolean.opBoolean","INTERSECT",EDGE,{"derivedFrom":[makeQuery(id+"F20.opExtrude","SWEPT_FACE",FACE,{"disambiguationData":[OSD([sQuery(id+"F19.wireOp",EDGE,"E13")])]}),makeQuery(id+"F22.opExtrude","SWEPT_FACE",FACE,{"disambiguationData":[OSD([sQuery(id+"F21.wireOp",EDGE,"E14")])]})]});
            var Q2;
            Q2=makeQuery(id+"F20.boolean.opBoolean","INTERSECT",EDGE,{"derivedFrom":[makeQuery(id+"F18.opExtrude","SWEPT_FACE",FACE,{"disambiguationData":[OSD([sQuery(id+"F17.wireOp",EDGE,"E12")])]}),makeQuery(id+"F20.opExtrude","SWEPT_FACE",FACE,{"disambiguationData":[OSD([sQuery(id+"F19.wireOp",EDGE,"E13")])]})]});
            var Q3;
            Q3=makeQuery(id+"F18.boolean.opBoolean","INTERSECT",EDGE,{"derivedFrom":[makeQuery(id+"F16.opExtrude","SWEPT_FACE",FACE,{"disambiguationData":[OSD([sQuery(id+"F15.wireOp",EDGE,"E11")])]}),makeQuery(id+"F18.opExtrude","SWEPT_FACE",FACE,{"disambiguationData":[OSD([sQuery(id+"F17.wireOp",EDGE,"E12")])]})]});
            var Q4;
            Q4=makeQuery(id+"F32.boolean.opBoolean","INTERSECT",EDGE,{"derivedFrom":[makeQuery(id+"F16.opExtrude","SWEPT_FACE",FACE,{"disambiguationData":[OSD([sQuery(id+"F15.wireOp",EDGE,"E11")])]}),makeQuery(id+"F32.opExtrude","SWEPT_FACE",FACE,{"disambiguationData":[OSD([sQuery(id+"F31.wireOp",EDGE,"E16")])]})]});
            var Q5;
            {var subQ0=sQuery(id+"F11.wireOp",EDGE,"E9");var subQ1=makeQuery(id+"F12.opExtrude","SWEPT_FACE",FACE,{"disambiguationData":[OSD([subQ0])]});var subQ2=makeQuery(id+"F14.opExtrude","SWEPT_FACE",FACE,{"disambiguationData":[OSD([sQuery(id+"F13.wireOp",EDGE,"E10")])]});Q5=makeQuery(id+"F35.boolean.opBoolean","SPLIT",EDGE,{"disambiguationData":[TD([subQ1,subQ2,makeQuery(id+"F26.opRevolve","SWEPT_FACE",FACE,{"disambiguationData":[OSD([subQ0])]}),makeQuery(id+"F32.opExtrude","SWEPT_FACE",FACE,{"disambiguationData":[OSD([sQuery(id+"F31.wireOp",EDGE,"E16")])]}),makeQuery(id+"F35.opRevolve","SWEPT_FACE",FACE,{"disambiguationData":[OSD([sQuery(id+"F33.wireOp",EDGE,"E18.top")])]}),makeQuery(id+"F35.opRevolve","SWEPT_FACE",FACE,{"disambiguationData":[OSD([sQuery(id+"F33.wireOp",EDGE,"E18.left")])]})]),OD(0.0)],"derivedFrom":makeQuery(id+"F14.boolean.opBoolean","INTERSECT",EDGE,{"derivedFrom":[subQ1,subQ2]})});}
            var Q6;
            {var subQ0=sQuery(id+"F11.wireOp",EDGE,"E9");var subQ1=makeQuery(id+"F12.opExtrude","SWEPT_FACE",FACE,{"disambiguationData":[OSD([subQ0])]});var subQ2=makeQuery(id+"F14.opExtrude","SWEPT_FACE",FACE,{"disambiguationData":[OSD([sQuery(id+"F13.wireOp",EDGE,"E10")])]});Q6=makeQuery(id+"F35.boolean.opBoolean","SPLIT",EDGE,{"disambiguationData":[TD([subQ1,subQ2,makeQuery(id+"F26.opRevolve","SWEPT_FACE",FACE,{"disambiguationData":[OSD([subQ0])]}),makeQuery(id+"F32.opExtrude","SWEPT_FACE",FACE,{"disambiguationData":[OSD([sQuery(id+"F31.wireOp",EDGE,"E16")])]}),makeQuery(id+"F35.opRevolve","SWEPT_FACE",FACE,{"disambiguationData":[OSD([sQuery(id+"F33.wireOp",EDGE,"E18.top")])]}),makeQuery(id+"F35.opRevolve","SWEPT_FACE",FACE,{"disambiguationData":[OSD([sQuery(id+"F33.wireOp",EDGE,"E18.left")])]})]),OD(1.0)],"derivedFrom":makeQuery(id+"F14.boolean.opBoolean","INTERSECT",EDGE,{"derivedFrom":[subQ1,subQ2]})});}
            var Q7;
            Q7=makeQuery(id+"F34.boolean.opBoolean","SPLIT",EDGE,{"disambiguationData":[OD(0.0)],"derivedFrom":makeQuery(id+"F12.boolean.opBoolean","INTERSECT",EDGE,{"derivedFrom":[makeQuery(id+"F10.opExtrude","SWEPT_FACE",FACE,{"disambiguationData":[OSD([sQuery(id+"F9.wireOp",EDGE,"E8")])]}),makeQuery(id+"F12.opExtrude","SWEPT_FACE",FACE,{"disambiguationData":[OSD([sQuery(id+"F11.wireOp",EDGE,"E9")])]})]})});
            fillet(context, id + "F47", {"entities" : qUnion([Q0, Q1, Q2, Q3, Q4, Q5, Q6, Q7]), "radius" : 10 * mm, "tangentPropagation" : true, "allowEdgeOverflow" : false});
        }
        {
            var Q0;
            Q0=makeQuery(id+"F32.opExtrude","CAP_EDGE",EDGE,{"disambiguationData":[OSD([sQuery(id+"F31.wireOp",EDGE,"E16")])],"isStart":false});
            fillet(context, id + "F48", {"entities" : qUnion([Q0]), "radius" : 10 * mm, "tangentPropagation" : true, "allowEdgeOverflow" : false});
        }
        {
            var Q0;
            {var subQ0=sQuery(id+"F11.wireOp",EDGE,"E9");Q0=makeQuery(id+"F37.boolean.opBoolean","INTERSECT",EDGE,{"derivedFrom":[makeQuery(id+"F34.boolean.opBoolean","SPLIT",FACE,{"disambiguationData":[TD([makeQuery(id+"F14.opExtrude","SWEPT_FACE",FACE,{"disambiguationData":[OSD([sQuery(id+"F13.wireOp",EDGE,"E10")])]})])],"derivedFrom":makeQuery(id+"F12.opExtrude","SWEPT_FACE",FACE,{"disambiguationData":[OSD([subQ0])]})}),makeQuery(id+"F37.opExtrude","SWEPT_FACE",FACE,{"disambiguationData":[OSD([sQuery(id+"F36.wireOp",EDGE,"E31.right")])]})]});}
            chamfer(context, id + "F49", {"entities" : qUnion([Q0]), "width" : 10 * mm, "tangentPropagation" : true});
        }
    });
